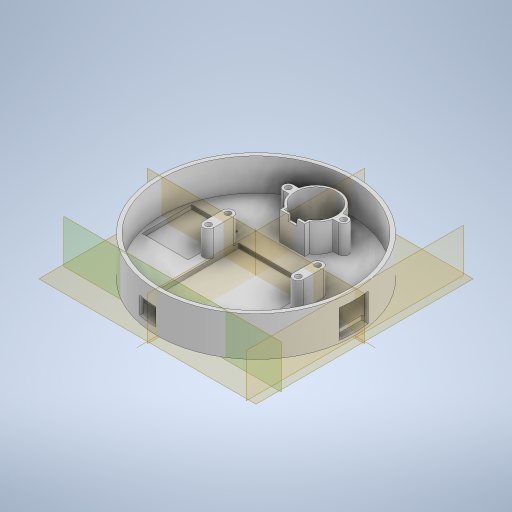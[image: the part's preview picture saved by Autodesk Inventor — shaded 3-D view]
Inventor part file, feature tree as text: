
AUTODESK INVENTOR PART (.ipt)
format: ipt  version: 2023 (Build 270158000, 158)  size: 454,144 bytes
history: native  units: in
note: dims shown in document units (in); Inventor stores cm internally (conversion verified against a paired STEP export)
features: extrude x11, sketch x11, plane x2
ambient origin geometry x8: Origin, YZ Plane, XZ Plane, XY Plane, X Axis, Y Axis, Z Axis, Center Point
bodies: Solid1 (feature_tree)
feature tree (24):
  extrude  "Extrusion1"  Depth=1.0827in TaperAngle=0.0deg
  extrude  "Extrusion2"  Depth=0.8858in TaperAngle=0.0deg
  extrude  "Extrusion3"  Depth=1.122in
  extrude  "Extrusion4"  Depth=0.689in
  extrude  "Extrusion5"  Depth=0.5709in
  extrude  "Extrusion6"  Depth=0.1181in
  extrude  "Extrusion7"  Depth=0.1575in TaperAngle=0.0deg
  extrude  "Extrusion8"  Depth=0.1575in
  plane  "Work Plane1"
  extrude  "Extrusion9"  Depth=0.748in
  plane  "Work Plane2"
  extrude  "Extrusion10"  Depth=1.2598in
  extrude  "Extrusion11"  Depth=1.3583in
  sketch  "Sketch1"  dims[d0=5.4134in d2=1.0827in d3=0.0in]
  sketch  "Sketch2"  dims[d4=5.1969in d5=0.8858in d6=0.0in]
  sketch  "Sketch3"  dims[d7=1.063in d8=1.122in]
  sketch  "Sketch4"  dims[d9=1.2402in d12=0.689in]
  sketch  "Sketch5"  dims[d14=0.0984in d15=0.5709in]
  sketch  "Sketch6"  dims[d16=0.7677in d17=0.0in d18=0.1181in]
  sketch  "Sketch7"  dims[d19=0.2362in d20=0.1575in d21=0.0in]
  sketch  "Sketch8"  dims[d24=0.1575in d25=0.1575in]
  sketch  "Sketch9"  dims[d26=0.748in d27=0.0in d28=1.1811in]
  sketch  "Sketch10"  dims[d29=0.6791in d30=1.2598in]
  sketch  "Sketch11"  dims[d31=90.0deg d32=1.3583in d33=0.1083in d34=0.0in d36=0.1476in d37=0.4134in d38=0.8268in d39=2.4606in d40=0.4134in d41=0.8268in d42=90.0deg d43=0.2953in d44=0.7087in d45=0.0in d46=0.4134in d47=2.126in d48=2.7008in d49=0.1181in d50=0.0in d52=0.4724in d53=0.4921in d54=4.0157in d55=0.0in d64=0.3937in d65=0.7874in d66=0.7874in d67=0.7874in d68=0.1969in d69=0.0in d70=0.1575in d71=0.1575in d72=0.1575in d73=0.1575in d74=0.4724in d75=0.0in]
